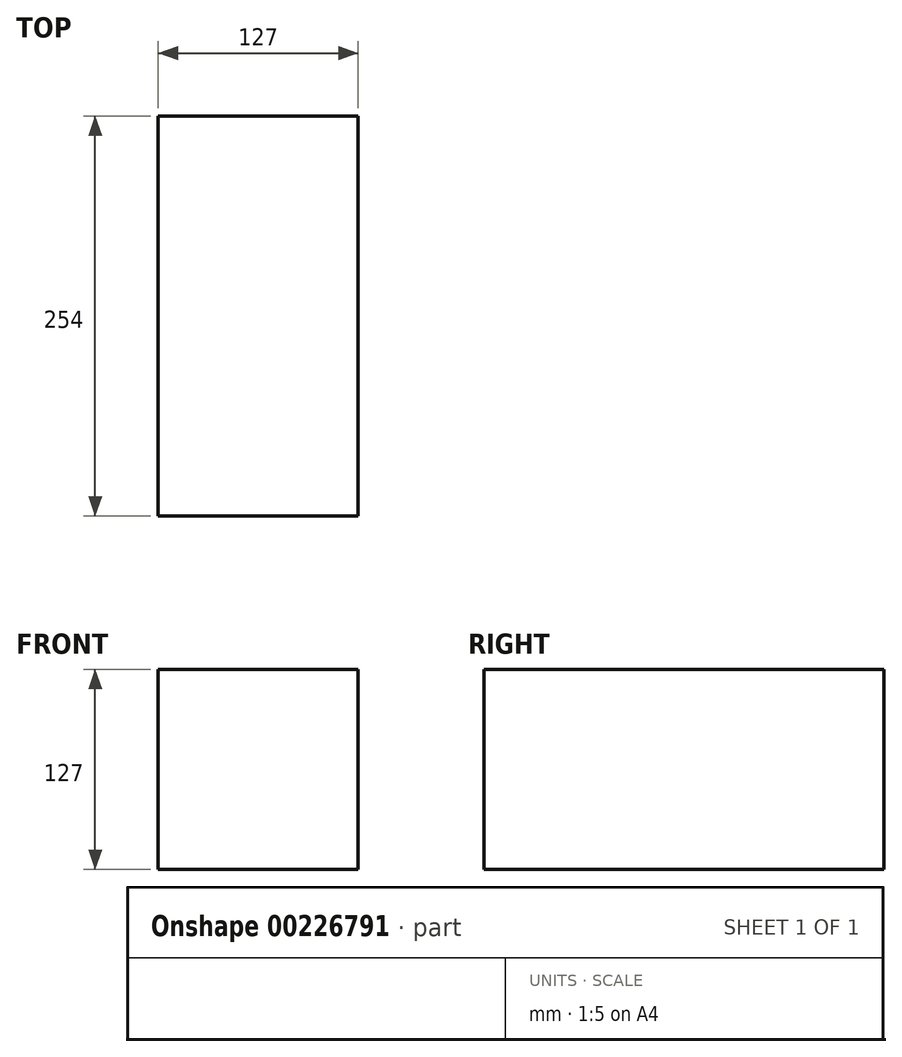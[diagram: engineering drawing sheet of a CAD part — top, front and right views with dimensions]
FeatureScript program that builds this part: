
annotation { "Feature Type Name" : "Feature", "Feature Type Description" : "" }
export const myFeature = defineFeature(function(context is Context, id is Id, definition is map)
    precondition{}
    {
        {
            var Q0;
            Q0=qCreatedBy(makeId("Front.planeOp"),FACE);
            var sketch = newSketch(context, id + "F0", { "sketchPlane" : qUnion([Q0])});
            skLineSegment(sketch, "E0.bottom", {"start": v(-63.5, 63.5) * mm, "end": v(63.5, 63.5) * mm});
            skLineSegment(sketch, "E0.top", {"start": v(-63.5, -63.5) * mm, "end": v(63.5, -63.5) * mm});
            skLineSegment(sketch, "E0.left", {"start": v(-63.5, 63.5) * mm, "end": v(-63.5, -63.5) * mm});
            skLineSegment(sketch, "E0.right", {"start": v(63.5, 63.5) * mm, "end": v(63.5, -63.5) * mm});
            skSolve(sketch);
        }
        {
            var Q0;
            Q0 = qSketchRegion(id + "F0", true);
            extrude(context, id + "F1", {"entities" : qUnion([Q0]), "depth" : 254 * mm});
        }
    });
